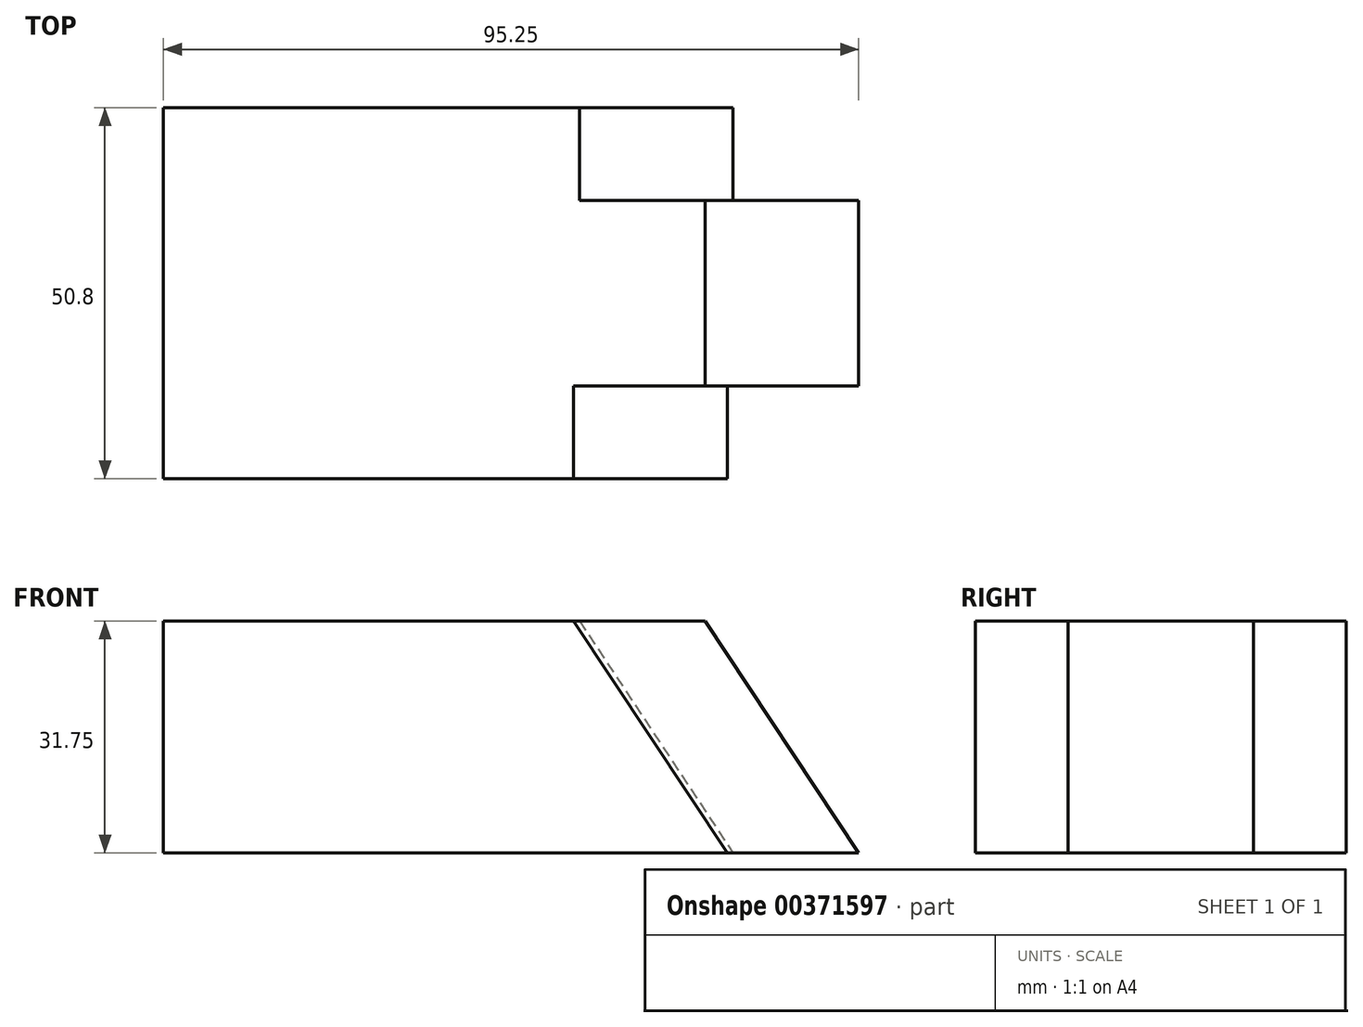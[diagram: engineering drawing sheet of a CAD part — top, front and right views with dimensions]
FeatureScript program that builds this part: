
annotation { "Feature Type Name" : "Feature", "Feature Type Description" : "" }
export const myFeature = defineFeature(function(context is Context, id is Id, definition is map)
    precondition{}
    {
        {
            var Q0;
            Q0=qCreatedBy(makeId("Front.planeOp"),FACE);
            var sketch = newSketch(context, id + "F0", { "sketchPlane" : qUnion([Q0])});
            skLineSegment(sketch, "E0", {"start": v(0, 0) * mm, "end": v(0, 31.75) * mm});
            skLineSegment(sketch, "E1", {"start": v(0, 31.75) * mm, "end": v(95.25, 31.75) * mm});
            skLineSegment(sketch, "E2", {"start": v(95.25, 31.75) * mm, "end": v(95.25, 0) * mm});
            skLineSegment(sketch, "E3", {"start": v(95.25, 0) * mm, "end": v(0, 0) * mm});
            skSolve(sketch);
        }
        {
            var Q0;
            Q0 = qSketchRegion(id + "F0", true);
            extrude(context, id + "F1", {"entities" : qUnion([Q0]), "depth" : 50.8 * mm});
        }
        {
            var Q0;
            Q0=makeQuery(id+"F1.opExtrude","CAP_FACE",FACE,{"disambiguationData":[OSD([sQuery(id+"F0.wireOp",EDGE,"E0"),sQuery(id+"F0.wireOp",EDGE,"E1"),sQuery(id+"F0.wireOp",EDGE,"E2"),sQuery(id+"F0.wireOp",EDGE,"E3")])],"isStart":false});
            var sketch = newSketch(context, id + "F2", { "sketchPlane" : qUnion([Q0])});
            skLineSegment(sketch, "E4", {"start": v(74.19, 31.75) * mm, "end": v(95.25, 0) * mm});
            skSolve(sketch);
        }
        {
            var Q0;
            {var subQ0=sQuery(id+"F2.wireOp",EDGE,"E4");Q0=makeQuery(id+"F2.imprint","IMPRINT",FACE,{"disambiguationData":[TD([[makeQuery(id+"F2.imprint","IMPRINT",EDGE,{"derivedFrom":subQ0}),1.0]])]});}
            extrude(context, id + "F3", {"entities" : qUnion([Q0]), "operationType" : NewBodyOperationType.REMOVE, "oppositeDirection" : true, "depth" : 50.8 * mm});
        }
        {
            var Q0;
            Q0=makeQuery(id+"F1.opExtrude","CAP_FACE",FACE,{"disambiguationData":[OSD([sQuery(id+"F0.wireOp",EDGE,"E0"),sQuery(id+"F0.wireOp",EDGE,"E1"),sQuery(id+"F0.wireOp",EDGE,"E2"),sQuery(id+"F0.wireOp",EDGE,"E3")])],"isStart":false});
            var sketch = newSketch(context, id + "F4", { "sketchPlane" : qUnion([Q0])});
            skLineSegment(sketch, "E5", {"start": v(56.2, 31.75) * mm, "end": v(77.26, 0) * mm});
            skSolve(sketch);
        }
        {
            var Q0;
            {var subQ0=sQuery(id+"F4.wireOp",EDGE,"E5");Q0=makeQuery(id+"F4.imprint","IMPRINT",FACE,{"disambiguationData":[TD([[makeQuery(id+"F4.imprint","IMPRINT",EDGE,{"derivedFrom":subQ0}),1.0]])]});}
            extrude(context, id + "F5", {"entities" : qUnion([Q0]), "operationType" : NewBodyOperationType.REMOVE, "oppositeDirection" : true, "depth" : 12.7 * mm});
        }
        {
            var Q0;
            Q0=makeQuery(id+"F1.opExtrude","CAP_FACE",FACE,{"disambiguationData":[OSD([sQuery(id+"F0.wireOp",EDGE,"E0"),sQuery(id+"F0.wireOp",EDGE,"E1"),sQuery(id+"F0.wireOp",EDGE,"E2"),sQuery(id+"F0.wireOp",EDGE,"E3")])],"isStart":true});
            var sketch = newSketch(context, id + "F6", { "sketchPlane" : qUnion([Q0])});
            skLineSegment(sketch, "E6", {"start": v(-56.98, 31.75) * mm, "end": v(-78.04, 0) * mm});
            skSolve(sketch);
        }
        {
            var Q0;
            {var subQ0=sQuery(id+"F6.wireOp",EDGE,"E6");Q0=makeQuery(id+"F6.imprint","IMPRINT",FACE,{"disambiguationData":[TD([[makeQuery(id+"F6.imprint","IMPRINT",EDGE,{"derivedFrom":subQ0}),-1.0]])]});}
            extrude(context, id + "F7", {"entities" : qUnion([Q0]), "operationType" : NewBodyOperationType.REMOVE, "oppositeDirection" : true, "depth" : 12.7 * mm});
        }
    });
